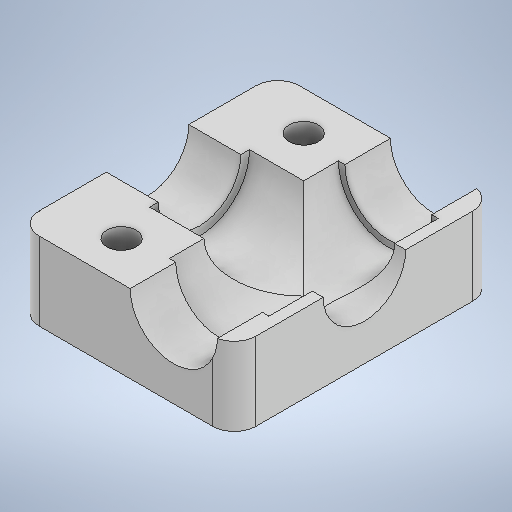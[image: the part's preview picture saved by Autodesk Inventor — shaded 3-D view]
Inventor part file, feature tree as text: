
AUTODESK INVENTOR PART (.ipt)
format: ipt  version: 2025 (Build 290162000, 162)  size: 301,568 bytes
history: native  units: mm
features: sketch x6, extrude x5, plane x1, hole x1, fillet x1
ambient origin geometry x8: Origin, YZ Plane, XZ Plane, XY Plane, X Axis, Y Axis, Z Axis, Center Point
bodies: Solid1 (feature_tree)
feature tree (14):
  extrude  "Extrusion1"  Depth=60.0mm
  extrude  "Extrusion2"  Depth=18.0mm
  extrude  "Extrusion3"  Depth=20.0mm
  extrude  "Extrusion4"  TaperAngle=0.0deg  [1 undecoded]
  plane  "Work Plane2"
  extrude  "Extrusion5"  Depth=39.0mm TaperAngle=0.0deg
  hole  "Hole2"  [1 undecoded]
  fillet  "Fillet1"  Radius=9.0mm
  sketch  "Sketch1"  dims[d0=50.0mm d1=60.0mm]
  sketch  "Sketch2"  dims[d2=18.0mm d3=0.0mm d4=19.0mm]
  sketch  "Sketch3"  dims[d5=0.0mm d6=0.0mm d7=20.0mm]
  sketch  "Sketch4"  dims[d8=14.0mm d9=0.0mm d10=0.0mm]
  sketch  "Sketch5"  dims[d11=23.0mm d12=39.0mm d13=0.0mm]
  sketch  "Sketch7"  dims[d14=23.0mm d15=24.0mm d16=0.0mm d28=9.0mm d29=9.0mm d30=15.0mm d31=6.756mm d32=6.0mm d33=11.113mm d34=6.35mm d35=90.0deg d36=8.0mm d37=20.594885mm d38=5.0mm]
note: 2 required parameter values undecoded (feature->parameter linkage not recoverable at this tier; creation-order binding heuristic only, values carry confidence <= 0.55)
